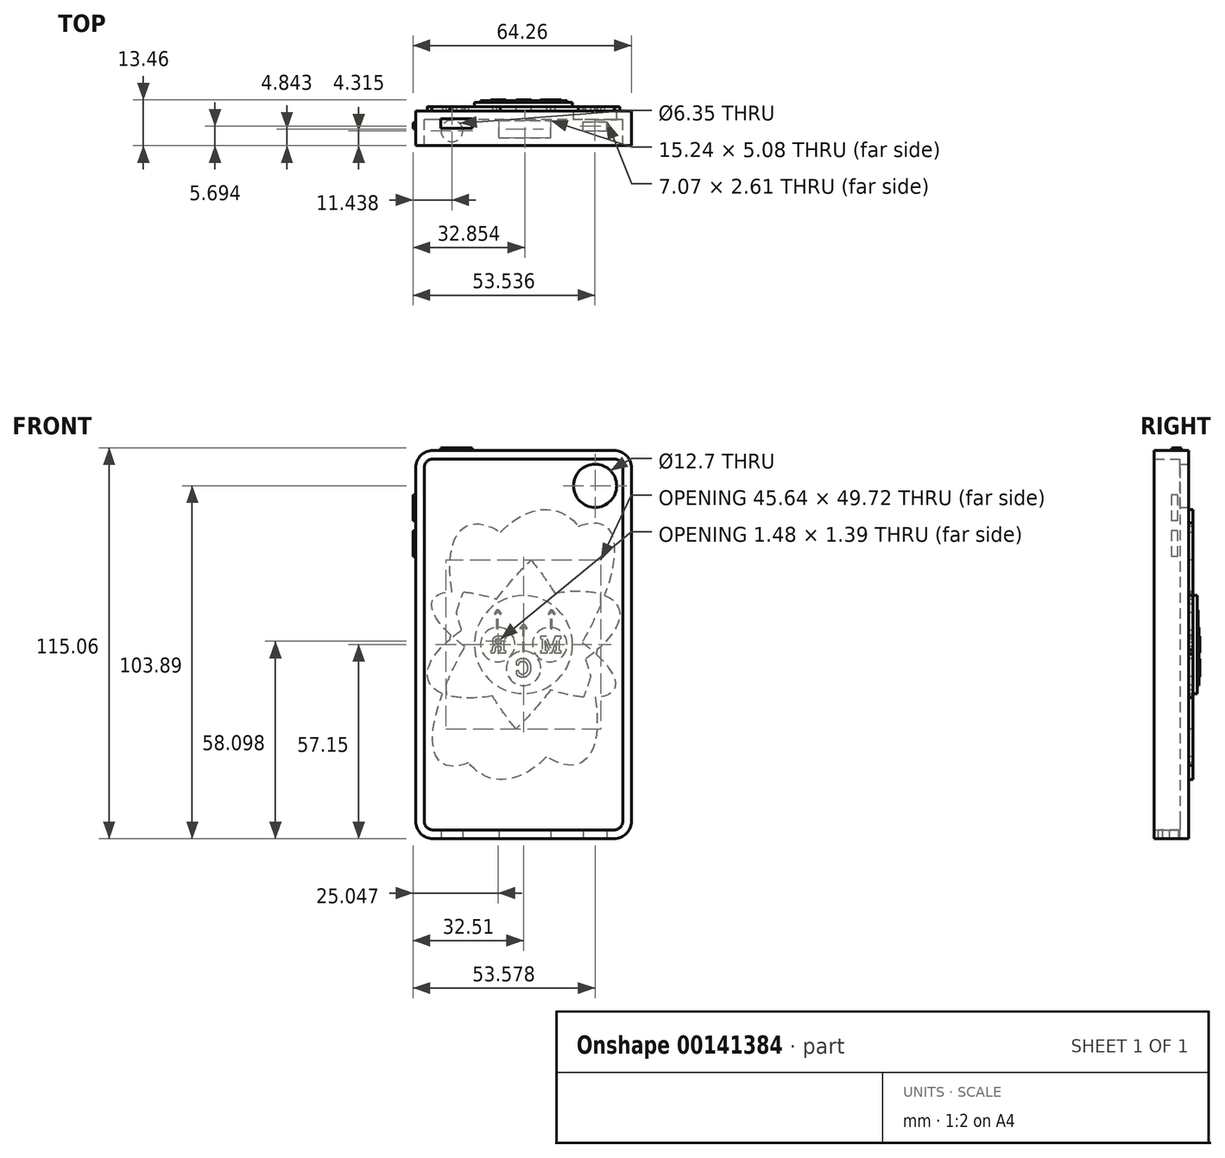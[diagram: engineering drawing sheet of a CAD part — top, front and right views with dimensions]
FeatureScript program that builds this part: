
annotation { "Feature Type Name" : "Feature", "Feature Type Description" : "" }
export const myFeature = defineFeature(function(context is Context, id is Id, definition is map)
    precondition{}
    {
        {
            var Q0;
            Q0=qCreatedBy(makeId("Front.planeOp"),FACE);
            var sketch = newSketch(context, id + "F0", { "sketchPlane" : qUnion([Q0])});
            skLineSegment(sketch, "E0.bottom", {"start": v(31.75, 57.15) * mm, "end": v(-31.75, 57.15) * mm});
            skLineSegment(sketch, "E0.top", {"start": v(31.75, -57.15) * mm, "end": v(-31.75, -57.15) * mm});
            skLineSegment(sketch, "E0.left", {"start": v(31.75, 57.15) * mm, "end": v(31.75, -57.15) * mm});
            skLineSegment(sketch, "E0.right", {"start": v(-31.75, 57.15) * mm, "end": v(-31.75, -57.15) * mm});
            skPoint(sketch, "E0.middle", {"position": v(0, 0) * mm});
            skSolve(sketch);
        }
        {
            var Q0;
            Q0 = qSketchRegion(id + "F0", true);
            extrude(context, id + "F1", {"entities" : qUnion([Q0]), "depth" : 10.16 * mm});
        }
        {
            var Q0;
            Q0=makeQuery(id+"F1.opExtrude","SWEPT_EDGE",EDGE,{"disambiguationData":[OSD([sQuery(id+"F0.wireOp",EDGE,"E0.bottom"),sQuery(id+"F0.wireOp",EDGE,"E0.right")])]});
            var Q1;
            Q1=makeQuery(id+"F1.opExtrude","SWEPT_EDGE",EDGE,{"disambiguationData":[OSD([sQuery(id+"F0.wireOp",EDGE,"E0.top"),sQuery(id+"F0.wireOp",EDGE,"E0.right")])]});
            var Q2;
            Q2=makeQuery(id+"F1.opExtrude","SWEPT_EDGE",EDGE,{"disambiguationData":[OSD([sQuery(id+"F0.wireOp",EDGE,"E0.bottom"),sQuery(id+"F0.wireOp",EDGE,"E0.left")])]});
            var Q3;
            Q3=makeQuery(id+"F1.opExtrude","SWEPT_EDGE",EDGE,{"disambiguationData":[OSD([sQuery(id+"F0.wireOp",EDGE,"E0.top"),sQuery(id+"F0.wireOp",EDGE,"E0.left")])]});
            fillet(context, id + "F2", {"entities" : qUnion([Q0, Q1, Q2, Q3]), "radius" : 5.08 * mm, "tangentPropagation" : true, "allowEdgeOverflow" : false});
        }
        {
            var Q0;
            Q0=makeQuery(id+"F1.opExtrude","CAP_FACE",FACE,{"disambiguationData":[OSD([sQuery(id+"F0.wireOp",EDGE,"E0.bottom"),sQuery(id+"F0.wireOp",EDGE,"E0.top"),sQuery(id+"F0.wireOp",EDGE,"E0.left"),sQuery(id+"F0.wireOp",EDGE,"E0.right")])],"isStart":false});
            shell(context, id + "F3", {"entities" : qUnion([Q0]), "thickness" : 2.54 * mm});
        }
        {
            var Q0;
            Q0=makeQuery(id+"F1.opExtrude","CAP_FACE",FACE,{"disambiguationData":[OSD([sQuery(id+"F0.wireOp",EDGE,"E0.bottom"),sQuery(id+"F0.wireOp",EDGE,"E0.top"),sQuery(id+"F0.wireOp",EDGE,"E0.left"),sQuery(id+"F0.wireOp",EDGE,"E0.right")])],"isStart":true});
            var sketch = newSketch(context, id + "F4", { "sketchPlane" : qUnion([Q0])});
            skEllipse(sketch, "E1", {"center": v(0, 0) * mm, "majorRadius": 40.5 * mm, "minorRadius": 21.5 * mm, "majorAxis": v(-0.22, 0.97)});
            skEllipse(sketch, "E2", {"center": v(0, 0) * mm, "majorRadius": 38.71 * mm, "minorRadius": 15.3 * mm, "majorAxis": v(0.43, 0.9)});
            skEllipse(sketch, "E3", {"center": v(0, 0) * mm, "majorRadius": 29.97 * mm, "minorRadius": 12.27 * mm, "majorAxis": v(-0.93, 0.36)});
            skEllipse(sketch, "E4", {"center": v(0, 0) * mm, "majorRadius": 42.37 * mm, "minorRadius": 14.3 * mm, "majorAxis": v(-0.57, 0.82)});
            skEllipse(sketch, "E5", {"center": v(0, 0) * mm, "majorRadius": 29.74 * mm, "minorRadius": 9.48 * mm, "majorAxis": v(0.9, 0.44)});
            skEllipse(sketch, "E6", {"center": v(0, 0) * mm, "majorRadius": 15.27 * mm, "minorRadius": 7.76 * mm, "majorAxis": v(-1, 0)});
            skSolve(sketch);
        }
        {
            var Q0;
            Q0 = qSketchRegion(id + "F4", true);
            extrude(context, id + "F5", {"entities" : qUnion([Q0]), "depth" : 1.27 * mm});
        }
        {
            var Q0;
            Q0=makeQuery(id+"F5.opExtrude","CAP_FACE",FACE,{"disambiguationData":[OSD([sQuery(id+"F4.wireOp",EDGE,"E1"),sQuery(id+"F4.wireOp",EDGE,"E2"),sQuery(id+"F4.wireOp",EDGE,"E3"),sQuery(id+"F4.wireOp",EDGE,"E4"),sQuery(id+"F4.wireOp",EDGE,"E5")])],"isStart":false});
            var sketch = newSketch(context, id + "F6", { "sketchPlane" : qUnion([Q0])});
            skCircle(sketch, "E7", {"center": v(0, 0) * mm, "radius": 14.43 * mm});
            skCircle(sketch, "E8", {"center": v(0, 0) * mm, "radius": 8.47 * mm});
            skCircle(sketch, "E9", {"center": v(0, 0) * mm, "radius": 3.98 * mm});
            skSolve(sketch);
        }
        {
            var Q0;
            Q0 = qSketchRegion(id + "F6", true);
            var Q1;
            Q1=makeQuery(id+"F6.imprint","IMPRINT",FACE,{"disambiguationData":[TD([[makeQuery(id+"F6.imprint","IMPRINT",EDGE,{"derivedFrom":sQuery(id+"F6.wireOp",EDGE,"E8")}),1.0]])]});
            var Q2;
            Q2=makeQuery(id+"F6.imprint","IMPRINT",FACE,{"disambiguationData":[TD([[makeQuery(id+"F6.imprint","IMPRINT",EDGE,{"derivedFrom":sQuery(id+"F6.wireOp",EDGE,"E9")}),1.0]])]});
            extrude(context, id + "F7", {"entities" : qUnion([Q0, Q1, Q2]), "depth" : 1.27 * mm});
        }
        {
            var Q0;
            Q0=makeQuery(id+"F1.opExtrude","CAP_FACE",FACE,{"disambiguationData":[OSD([sQuery(id+"F0.wireOp",EDGE,"E0.bottom"),sQuery(id+"F0.wireOp",EDGE,"E0.top"),sQuery(id+"F0.wireOp",EDGE,"E0.left"),sQuery(id+"F0.wireOp",EDGE,"E0.right")])],"isStart":true});
            var sketch = newSketch(context, id + "F8", { "sketchPlane" : qUnion([Q0])});
            skCircle(sketch, "E10", {"center": v(-21.07, 46.74) * mm, "radius": 6.35 * mm});
            skSolve(sketch);
        }
        {
            var Q0;
            Q0 = qSketchRegion(id + "F8", true);
            extrude(context, id + "F9", {"entities" : qUnion([Q0]), "operationType" : NewBodyOperationType.REMOVE, "oppositeDirection" : true, "depth" : 25.4 * mm});
        }
        {
            var Q0;
            Q0=makeQuery(id+"F1.opExtrude","SWEPT_FACE",FACE,{"disambiguationData":[OSD([sQuery(id+"F0.wireOp",EDGE,"E0.bottom")])]});
            var sketch = newSketch(context, id + "F10", { "sketchPlane" : qUnion([Q0])});
            skLineSegment(sketch, "E11.bottom", {"start": v(-15.07, -5.02) * mm, "end": v(-24.38, -5.02) * mm});
            skLineSegment(sketch, "E11.top", {"start": v(-15.07, -2.23) * mm, "end": v(-24.38, -2.23) * mm});
            skLineSegment(sketch, "E11.left", {"start": v(-15.07, -5.02) * mm, "end": v(-15.07, -2.23) * mm});
            skLineSegment(sketch, "E11.right", {"start": v(-24.38, -5.02) * mm, "end": v(-24.38, -2.23) * mm});
            skSolve(sketch);
        }
        {
            var Q0;
            Q0 = qSketchRegion(id + "F10", true);
            extrude(context, id + "F11", {"entities" : qUnion([Q0]), "operationType" : NewBodyOperationType.ADD, "depth" : 0.76 * mm});
        }
        {
            var Q0;
            Q0=makeQuery(id+"F1.opExtrude","SWEPT_FACE",FACE,{"disambiguationData":[OSD([sQuery(id+"F0.wireOp",EDGE,"E0.right")])]});
            var sketch = newSketch(context, id + "F12", { "sketchPlane" : qUnion([Q0])});
            skLineSegment(sketch, "E12.bottom", {"start": v(3.4, 44.07) * mm, "end": v(5.16, 44.07) * mm});
            skLineSegment(sketch, "E12.top", {"start": v(3.4, 36.45) * mm, "end": v(5.16, 36.45) * mm});
            skLineSegment(sketch, "E12.left", {"start": v(3.4, 44.07) * mm, "end": v(3.4, 36.45) * mm});
            skLineSegment(sketch, "E12.right", {"start": v(5.16, 44.07) * mm, "end": v(5.16, 36.45) * mm});
            skLineSegment(sketch, "E13.bottom", {"start": v(3.4, 33.52) * mm, "end": v(5.16, 33.52) * mm});
            skLineSegment(sketch, "E13.top", {"start": v(3.4, 25.9) * mm, "end": v(5.16, 25.9) * mm});
            skLineSegment(sketch, "E13.left", {"start": v(3.4, 33.52) * mm, "end": v(3.4, 25.9) * mm});
            skLineSegment(sketch, "E13.right", {"start": v(5.16, 33.52) * mm, "end": v(5.16, 25.9) * mm});
            skSolve(sketch);
        }
        {
            var Q0;
            Q0 = qSketchRegion(id + "F12", true);
            extrude(context, id + "F13", {"entities" : qUnion([Q0]), "operationType" : NewBodyOperationType.ADD, "depth" : 0.76 * mm});
        }
        {
            var Q0;
            Q0=makeQuery(id+"F1.opExtrude","SWEPT_FACE",FACE,{"disambiguationData":[OSD([sQuery(id+"F0.wireOp",EDGE,"E0.top")])]});
            var sketch = newSketch(context, id + "F14", { "sketchPlane" : qUnion([Q0])});
            skLineSegment(sketch, "E14.bottom", {"start": v(-7.28, 7.86) * mm, "end": v(7.96, 7.86) * mm});
            skLineSegment(sketch, "E14.top", {"start": v(-7.28, 2.78) * mm, "end": v(7.96, 2.78) * mm});
            skLineSegment(sketch, "E14.left", {"start": v(-7.28, 7.86) * mm, "end": v(-7.28, 2.78) * mm});
            skLineSegment(sketch, "E14.right", {"start": v(7.96, 7.86) * mm, "end": v(7.96, 2.78) * mm});
            skCircle(sketch, "E15", {"center": v(-21.07, 5.85) * mm, "radius": 3.18 * mm});
            skPoint(sketch, "E15.first.point", {"position": v(-23.91, 7.27) * mm});
            skPoint(sketch, "E15.second.point", {"position": v(-18.78, 3.65) * mm});
            skPoint(sketch, "E15.third.point", {"position": v(-23, 3.33) * mm});
            skLineSegment(sketch, "E16.bottom", {"start": v(17.5, 5.77) * mm, "end": v(24.56, 5.77) * mm});
            skLineSegment(sketch, "E16.top", {"start": v(17.5, 3.16) * mm, "end": v(24.56, 3.16) * mm});
            skLineSegment(sketch, "E16.left", {"start": v(17.5, 5.77) * mm, "end": v(17.5, 3.16) * mm});
            skLineSegment(sketch, "E16.right", {"start": v(24.56, 5.77) * mm, "end": v(24.56, 3.16) * mm});
            skSolve(sketch);
        }
        {
            var Q0;
            Q0 = qSketchRegion(id + "F14", true);
            extrude(context, id + "F15", {"entities" : qUnion([Q0]), "operationType" : NewBodyOperationType.REMOVE, "oppositeDirection" : true, "depth" : 12.7 * mm});
        }
        {
            var Q0;
            Q0 = qSketchRegion(id + "F14", true);
            extrude(context, id + "F16", {"entities" : qUnion([Q0]), "operationType" : NewBodyOperationType.REMOVE, "oppositeDirection" : true, "depth" : 12.7 * mm});
        }
        {
            var Q0;
            Q0=makeQuery(id+"F7.opExtrude","CAP_FACE",FACE,{"disambiguationData":[OSD([sQuery(id+"F6.wireOp",EDGE,"E7")])],"isStart":false});
            var sketch = newSketch(context, id + "F17", { "sketchPlane" : qUnion([Q0])});
            skCircle(sketch, "E17", {"center": v(0, -6.98) * mm, "radius": 5.08 * mm});
            skCircle(sketch, "E18", {"center": v(7.57, 0) * mm, "radius": 5.08 * mm});
            skCircle(sketch, "E19", {"center": v(-7.73, 0) * mm, "radius": 5.08 * mm});
            skLineSegment(sketch, "E20", {"start": v(0, -1.9) * mm, "end": v(0, 7.07) * mm});
            skLineSegment(sketch, "E21", {"start": v(0, 7.07) * mm, "end": v(1.86, 5.2) * mm});
            skLineSegment(sketch, "E22", {"start": v(0, 7.07) * mm, "end": v(-1.67, 5.4) * mm});
            skLineSegment(sketch, "E23", {"start": v(7.07, 5.06) * mm, "end": v(7.07, 9.3) * mm});
            skLineSegment(sketch, "E24", {"start": v(7.07, 9.3) * mm, "end": v(5.18, 7.48) * mm});
            skLineSegment(sketch, "E25", {"start": v(7.07, 9.3) * mm, "end": v(9.12, 7.18) * mm});
            skLineSegment(sketch, "E26", {"start": v(-7.23, 5.05) * mm, "end": v(-7.23, 9.3) * mm});
            skLineSegment(sketch, "E27", {"start": v(-7.23, 9.3) * mm, "end": v(-9.3, 7.26) * mm});
            skLineSegment(sketch, "E28", {"start": v(-7.23, 9.3) * mm, "end": v(-5.4, 7.44) * mm});
            skPoint(sketch, "E29", {"position": v(7.07, 7.18) * mm});
            skLineSegment(sketch, "E30.bottom", {"start": v(-7.23, 5.05) * mm, "end": v(-7.23, 5.05) * mm});
            skLineSegment(sketch, "E30.top", {"start": v(-7.23, 9.3) * mm, "end": v(-7.23, 9.3) * mm});
            skPoint(sketch, "E30.middle", {"position": v(-7.23, 7.18) * mm});
            skSolve(sketch);
        }
        {
            var Q0;
            Q0 = qSketchRegion(id + "F17", true);
            extrude(context, id + "F18", {"entities" : qUnion([Q0]), "depth" : 0.5 * mm});
        }
        {
            var Q0;
            Q0=makeQuery(id+"F7.opExtrude","CAP_FACE",FACE,{"disambiguationData":[OSD([sQuery(id+"F6.wireOp",EDGE,"E7")])],"isStart":false});
            var sketch = newSketch(context, id + "F19", { "sketchPlane" : qUnion([Q0])});
            skLineSegment(sketch, "E31.bottom", {"start": v(-8.02, 4.66) * mm, "end": v(-8.4, 4.66) * mm});
            skLineSegment(sketch, "E31.top", {"start": v(-8.02, 10.24) * mm, "end": v(-8.4, 10.24) * mm});
            skLineSegment(sketch, "E31.left", {"start": v(-8.02, 4.66) * mm, "end": v(-8.02, 10.24) * mm});
            skLineSegment(sketch, "E31.right", {"start": v(-8.4, 4.66) * mm, "end": v(-8.4, 10.24) * mm});
            skPoint(sketch, "E31.middle", {"position": v(-8.21, 7.45) * mm});
            skLineSegment(sketch, "E32.bottom", {"start": v(0.14, -2.17) * mm, "end": v(-0.14, -2.17) * mm});
            skLineSegment(sketch, "E32.top", {"start": v(0.14, 5.96) * mm, "end": v(-0.14, 5.96) * mm});
            skLineSegment(sketch, "E32.left", {"start": v(0.14, -2.17) * mm, "end": v(0.14, 5.96) * mm});
            skLineSegment(sketch, "E32.right", {"start": v(-0.14, -2.17) * mm, "end": v(-0.14, 5.96) * mm});
            skPoint(sketch, "E32.middle", {"position": v(0, 1.9) * mm});
            skLineSegment(sketch, "E33.bottom", {"start": v(7.8, 4.66) * mm, "end": v(7.44, 4.66) * mm});
            skLineSegment(sketch, "E33.top", {"start": v(7.8, 10.24) * mm, "end": v(7.44, 10.24) * mm});
            skLineSegment(sketch, "E33.left", {"start": v(7.8, 4.66) * mm, "end": v(7.8, 10.24) * mm});
            skLineSegment(sketch, "E33.right", {"start": v(7.44, 4.66) * mm, "end": v(7.44, 10.24) * mm});
            skPoint(sketch, "E33.middle", {"position": v(7.62, 7.45) * mm});
            skPoint(sketch, "E33.middle.positionSnap0", {"position": v(-8.02, 7.45) * mm});
            skPoint(sketch, "E33.centerSnap0", {"position": v(-8.02, 7.45) * mm});
            skSolve(sketch);
        }
        {
            var Q0;
            Q0 = qSketchRegion(id + "F19", true);
            extrude(context, id + "F20", {"entities" : qUnion([Q0]), "depth" : 0.25 * mm});
        }
        {
            var Q0;
            Q0=makeQuery(id+"F18.opExtrude","CAP_FACE",FACE,{"disambiguationData":[OSD([sQuery(id+"F17.wireOp",EDGE,"E19")])],"isStart":false});
            var sketch = newSketch(context, id + "F21", { "sketchPlane" : qUnion([Q0])});
            skText(sketch, "E34", { "text": "M", "fontName": "RobotoSlab-Bold.ttf"});
            skText(sketch, "E35", { "text": "C ", "fontName": "RobotoSlab-Bold.ttf"});
            skText(sketch, "E36", { "text": "R", "fontName": "RobotoSlab-Bold.ttf"});
            const initialGuessF21  = {"E34": [-0.01124, -0.00245, 1, 0, 0.0049], "E35": [-0.0024, -0.00948, 1, 0, 0.00532], "E36": [0.00505, -0.00245, 1, 0, 0.0049]};
            skSetInitialGuess(sketch, initialGuessF21);
            skSolve(sketch);
        }
        {
            var Q0;
            Q0 = qSketchRegion(id + "F21", true);
            extrude(context, id + "F22", {"entities" : qUnion([Q0]), "depth" : 0.25 * mm});
        }
        {
            var Q0;
            Q0=makeQuery(id+"F7.opExtrude","CAP_FACE",FACE,{"disambiguationData":[OSD([sQuery(id+"F6.wireOp",EDGE,"E7")])],"isStart":false});
            var sketch = newSketch(context, id + "F23", { "sketchPlane" : qUnion([Q0])});
            skLineSegment(sketch, "E37.bottom", {"start": v(-8.12, 10) * mm, "end": v(-9.04, 8.78) * mm});
            skLineSegment(sketch, "E37.top", {"start": v(-8.37, 10.18) * mm, "end": v(-9.29, 8.97) * mm});
            skLineSegment(sketch, "E37.left", {"start": v(-8.12, 10) * mm, "end": v(-8.37, 10.18) * mm});
            skLineSegment(sketch, "E37.right", {"start": v(-9.04, 8.78) * mm, "end": v(-9.29, 8.97) * mm});
            skPoint(sketch, "E37.middle", {"position": v(-50.38, 9.84) * mm});
            skLineSegment(sketch, "E38.1.0.0", {"start": v(-8.05, 10.24) * mm, "end": v(-7.22, 8.97) * mm});
            skLineSegment(sketch, "E38.1.0.1", {"start": v(-8.31, 10.07) * mm, "end": v(-7.47, 8.8) * mm});
            skLineSegment(sketch, "E38.1.0.2", {"start": v(-7.22, 8.97) * mm, "end": v(-7.47, 8.8) * mm});
            skLineSegment(sketch, "E38.1.0.3", {"start": v(-8.05, 10.24) * mm, "end": v(-8.31, 10.07) * mm});
            skLineSegment(sketch, "E38.2.0.0", {"start": v(0.14, 5.75) * mm, "end": v(-0.78, 4.53) * mm});
            skLineSegment(sketch, "E38.2.0.1", {"start": v(-0.1, 5.93) * mm, "end": v(-1.03, 4.72) * mm});
            skLineSegment(sketch, "E38.2.0.2", {"start": v(-0.78, 4.53) * mm, "end": v(-1.03, 4.72) * mm});
            skLineSegment(sketch, "E38.2.0.3", {"start": v(0.14, 5.75) * mm, "end": v(-0.1, 5.93) * mm});
            skLineSegment(sketch, "E38.3.0.0", {"start": v(0.12, 5.99) * mm, "end": v(1.09, 4.81) * mm});
            skLineSegment(sketch, "E38.3.0.1", {"start": v(-0.12, 5.8) * mm, "end": v(0.85, 4.62) * mm});
            skLineSegment(sketch, "E38.3.0.2", {"start": v(1.09, 4.81) * mm, "end": v(0.85, 4.62) * mm});
            skLineSegment(sketch, "E38.3.0.3", {"start": v(0.12, 5.99) * mm, "end": v(-0.12, 5.8) * mm});
            skLineSegment(sketch, "E38.4.0.0", {"start": v(7.74, 10.05) * mm, "end": v(6.84, 8.82) * mm});
            skLineSegment(sketch, "E38.4.0.1", {"start": v(7.49, 10.23) * mm, "end": v(6.6, 9) * mm});
            skLineSegment(sketch, "E38.4.0.2", {"start": v(6.84, 8.82) * mm, "end": v(6.6, 9) * mm});
            skLineSegment(sketch, "E38.4.0.3", {"start": v(7.74, 10.05) * mm, "end": v(7.49, 10.23) * mm});
            skLineSegment(sketch, "E38.direction1", {"start": v(-9.2, 8.87) * mm, "end": v(-5.5, 8.87) * mm, "construction": true});
            skLineSegment(sketch, "E39.1.0.0", {"start": v(7.54, 10.11) * mm, "end": v(8.4, 8.85) * mm});
            skLineSegment(sketch, "E39.1.0.1", {"start": v(7.8, 10.29) * mm, "end": v(8.66, 9.03) * mm});
            skLineSegment(sketch, "E39.1.0.2", {"start": v(8.66, 9.03) * mm, "end": v(8.4, 8.85) * mm});
            skLineSegment(sketch, "E39.1.0.3", {"start": v(7.8, 10.29) * mm, "end": v(7.54, 10.11) * mm});
            skLineSegment(sketch, "E39.direction1", {"start": v(6.44, 8.88) * mm, "end": v(10.08, 8.93) * mm, "construction": true});
            skSolve(sketch);
        }
        {
            var Q0;
            {var subQ0=sQuery(id+"F23.wireOp",EDGE,"E38.1.0.0");Q0=makeQuery(id+"F23.imprint","IMPRINT",FACE,{"disambiguationData":[TD([[makeQuery(id+"F23.imprint","IMPRINT",EDGE,{"derivedFrom":subQ0}),-1.0]])]});}
            var Q1;
            {var subQ6=sQuery(id+"F23.wireOp",EDGE,"E37.top");Q1=makeQuery(id+"F23.imprint","IMPRINT",FACE,{"disambiguationData":[TD([[makeQuery(id+"F23.imprint","IMPRINT",EDGE,{"derivedFrom":subQ6}),1.0]])]});}
            var Q2;
            {var subQ1=sQuery(id+"F23.wireOp",EDGE,"E38.2.0.1");Q2=makeQuery(id+"F23.imprint","IMPRINT",FACE,{"disambiguationData":[TD([[makeQuery(id+"F23.imprint","IMPRINT",EDGE,{"derivedFrom":subQ1}),1.0]])]});}
            var Q3;
            {var subQ4=sQuery(id+"F23.wireOp",EDGE,"E38.3.0.0");Q3=makeQuery(id+"F23.imprint","IMPRINT",FACE,{"disambiguationData":[TD([[makeQuery(id+"F23.imprint","IMPRINT",EDGE,{"derivedFrom":subQ4}),-1.0]])]});}
            var Q4;
            {var subQ1=sQuery(id+"F23.wireOp",EDGE,"E38.4.0.1");Q4=makeQuery(id+"F23.imprint","IMPRINT",FACE,{"disambiguationData":[TD([[makeQuery(id+"F23.imprint","IMPRINT",EDGE,{"derivedFrom":subQ1}),1.0]])]});}
            var Q5;
            {var subQ6=sQuery(id+"F23.wireOp",EDGE,"E39.1.0.1");Q5=makeQuery(id+"F23.imprint","IMPRINT",FACE,{"disambiguationData":[TD([[makeQuery(id+"F23.imprint","IMPRINT",EDGE,{"derivedFrom":subQ6}),-1.0]])]});}
            extrude(context, id + "F24", {"entities" : qUnion([Q0, Q1, Q2, Q3, Q4, Q5]), "depth" : 0.25 * mm});
        }
    });
